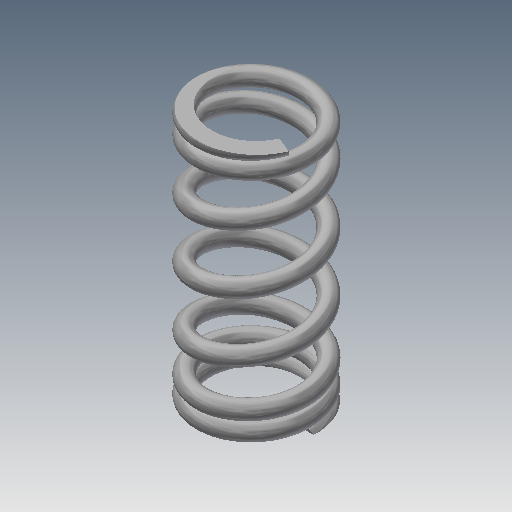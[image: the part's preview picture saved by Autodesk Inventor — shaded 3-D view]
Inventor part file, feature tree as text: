
AUTODESK INVENTOR PART (.ipt)
format: ipt  version: 2017 (Build 210142000, 142)  size: 893,952 bytes
history: native  units: mm
features: other x67, extrude x8, helix x5, sketch x3, sweep x2, plane x1
ambient origin geometry x8: Origin, YZ Plane, XZ Plane, XY Plane, X Axis, Y Axis, Z Axis, Center Point
bodies: Solid1 (feature_tree)
feature tree (86):
  other  "Main Coil Path(Right)"
  other  "Section Work Plane(Right)"
  other  "Start Work Plane(Right)"
  other  "End Work Plane(Right)"
  other  "End Cut Work Plane(Right)"
  other  "Start Cut Work Plane(Right)"
  other  "Plain Ends Cut Work Plane 1(Right)"
  other  "Plain Ends Cut Work Plane 2(Right)"
  sweep  "Main Coil Feature(R)"
  other  "Start Transition Coil 1(Right)"
  helix  "Coil  Start Transition 2(R)"  [1 undecoded]
  helix  "Coil  Start Transition 3(R)"  [1 undecoded]
  helix  "Coil  Start Transition 4(R)"  [1 undecoded]
  other  "Start Ends Coil(Right)"
  extrude  "Start Cut Feature(Right)"  Depth=10.0mm
  other  "End Transition Coil 1(Right)"
  other  "End Transition Coil 2(Right)"
  other  "End Transition Coil 3(Right)"
  other  "End Transition Coil 4(Right)"
  other  "End Coil(Right)"
  extrude  "End Cut Feature(Right)"  Depth=10.0mm
  extrude  "Plain Ends Cut Feature 1(Right)"  Depth=10.0mm
  extrude  "Plain Ends Cut  2(R)"  Depth=10.0mm TaperAngle=0.0deg
  other  "Main Coil Path(Left)"
  other  "Section Work Plane(Left)"
  other  "Start Work Plane(Left)"
  other  "End Work Plane(Left)"
  other  "End Cut Work Plane(Left)"
  other  "Start Cut Work Plane(Left)"
  other  "Plain Ends Cut Work Plane 1(Left)"
  other  "Plain Ends Cut Work Plane 2(Left)"
  sweep  "Main Coil Feature(L)"
  other  "Start Transition Coil 1(Left)"
  other  "Start Transition Coil 2(Left)"
  other  "Start Transition Coil 3(Left)"
  other  "Start Transition Coil 4(Left)"
  other  "Start Ends Coil(Left)"
  extrude  "Start Cut Feature(Left)"  Depth=10.0mm TaperAngle=0.0deg
  other  "End Transition Coil 1(Left)"
  other  "End Transition Coil 2(Left)"
  other  "End Transition Coil 3(Left)"
  other  "End Transition Coil 4(Left)"
  other  "End Coil(Left)"
  extrude  "End Cut Feature(Left)"  Depth=10.0mm
  extrude  "Cut Plain Ends Cut 1(L)"  TaperAngle=0.0deg  [1 undecoded]
  extrude  "Cut Plain Ends Cut 2(L)"  TaperAngle=0.0deg  [1 undecoded]
  other  "iMate Based Work Plane"
  other  "Preview Center Point"
  other  "Preview X Axis"
  other  "Path Section Sketch(Right)"
  other  "Srf1"
  helix  "Coil Section Sketch(Right)"  [1 undecoded]
  other  "Start Transition Coil Sketch 1(Right)"
  sketch  "Sketch  Start Transition 2(R)"  dims[d0=0.25mm d2=3.484629mm d3=10.0mm d4=26.875mm]
  sketch  "Sketch  Start Transition 3(R)"  dims[d5=0.0mm d6=90.0deg d7=90.0deg d8=0.0mm d9=0.0mm d12=2.448943mm d13=-3.186113mm d14=1.0mm]
  sketch  "Sketch  Start Transition 4(R)"  dims[d15=0.0mm d16=2.863472mm d17=10.0mm d18=2.5mm d19=0.0mm d20=90.0deg d21=90.0deg d22=0.0mm d23=0.0mm d24=2.242315mm d25=10.0mm d26=2.5mm d27=0.0mm d28=90.0deg d29=90.0deg d30=0.0mm d31=0.0mm d32=1.621157mm d33=10.0mm d34=2.5mm d35=0.0mm d36=90.0deg d37=90.0deg d38=0.0mm d39=0.0mm d40=1.0mm d41=10.0mm d42=2.5mm d43=0.0mm d44=90.0deg d45=90.0deg d46=0.0mm d47=0.0mm d48=2.863472mm d49=10.0mm d50=1.875mm d51=0.0mm d52=90.0deg d53=90.0deg d54=0.0mm d55=0.0mm d56=2.242315mm d57=10.0mm d58=1.875mm d59=0.0mm d60=90.0deg d61=90.0deg d62=0.0mm d63=0.0mm d64=1.621157mm d65=10.0mm d66=1.875mm d67=0.0mm d68=90.0deg d69=90.0deg d70=0.0mm d71=0.0mm d72=1.0mm d73=10.0mm d74=1.875mm d75=0.0mm d76=90.0deg d77=90.0deg d78=0.0mm d79=0.0mm d81=10.0mm d82=15.0mm d83=0.0mm d84=90.0deg d85=90.0deg d86=0.0mm d87=0.0mm d88=1.016944mm d89=10.0mm d90=10.0mm d91=0.0mm d92=90.0deg d93=90.0deg d94=0.0mm d95=0.0mm d96=7.0mm d97=1.016944mm d98=0.0mm d99=7.0mm d100=1.016944mm d101=0.0mm d102=0.0mm d103=0.0mm d104=0.0mm d105=0.0mm d106=0.0mm d108=0.0mm d112=0.0mm d113=0.0mm d114=0.0mm d121=0.271039mm d131=0.0mm d132=0.0mm d133=0.0mm d134=0.0mm d135=0.25mm d137=3.484629mm d138=10.0mm d139=26.875mm d140=0.0mm d141=90.0deg d142=90.0deg d143=0.0mm d144=0.0mm d145=2.448943mm d146=-3.186113mm d147=0.271039mm d148=0.016803mm d149=1.0mm d150=0.0mm d151=0.0mm d152=2.863472mm d153=10.0mm d154=2.5mm d155=0.0mm d156=90.0deg d157=90.0deg d158=0.0mm d159=0.0mm d160=2.242315mm d161=10.0mm d162=2.5mm d163=0.0mm d164=90.0deg d165=90.0deg d166=0.0mm d167=0.0mm d168=1.621157mm d169=10.0mm d170=2.5mm d171=0.0mm d172=90.0deg d173=90.0deg d174=0.0mm d175=0.0mm d176=1.0mm d177=10.0mm d178=2.5mm d179=0.0mm d180=90.0deg d181=90.0deg d182=0.0mm d183=0.0mm d184=10.0mm d185=10.0mm d186=10.0mm d187=10.0mm d188=1.016944mm d189=10.0mm d190=15.0mm d191=0.0mm d192=90.0deg d193=90.0deg d194=0.0mm d195=0.0mm d196=10.0mm d197=7.0mm d198=1.016944mm d199=0.0mm d200=10.0mm d201=2.863472mm d202=10.0mm d203=1.875mm d204=0.0mm d205=90.0deg d206=90.0deg d207=0.0mm d208=0.0mm d209=10.0mm d210=2.242315mm d211=10.0mm d212=1.875mm d213=0.0mm d214=90.0deg d215=90.0deg d216=0.0mm d217=0.0mm d218=1.621157mm d219=10.0mm d220=1.875mm d221=0.0mm d222=90.0deg d223=90.0deg d224=0.0mm d225=0.0mm d226=1.0mm d227=10.0mm d228=1.875mm d229=0.0mm d230=90.0deg d231=90.0deg d232=0.0mm d233=0.0mm d234=10.0mm d235=10.0mm d236=10.0mm d237=1.016944mm d238=10.0mm d239=10.0mm d240=0.0mm d241=90.0deg d242=90.0deg d243=0.0mm d244=0.0mm d245=7.0mm d246=1.016944mm d247=0.0mm d248=10.0mm d249=10.0mm d254=7.0mm d255=10.0mm d256=0.0mm d257=20.0mm d258=-0.016803mm d259=7.0mm d260=10.0mm d261=0.0mm d262=10.0mm d263=7.0mm d264=10.0mm d265=0.0mm d266=10.0mm d267=0.0mm d270=-3.061113mm d271=0.0mm d272=7.0mm d273=10.0mm d274=0.0mm d275=20.0mm d276=-157.079633mm d277=6.0mm d278=6.0mm d279=0.0mm d280=0.0mm]
  other  "End Transition Coil Sketch 1(Right)"
  other  "End Transition Coil Sketch 2(Right)"
  other  "End Transition Coil Sketch 3(Right)"
  other  "End Transition Coil Sketch 4(Right)"
  other  "Start Ends Skecth(Right)"
  other  "End Coil Skecth(Right)"
  other  "End Cut Sketch(Right)"
  other  "Start Cut Sketch(Right)"
  other  "Path Section Sketch(Left)"
  other  "Srf2"
  helix  "Coil Section Sketch(Left)"  [1 undecoded]
  other  "Start Transition Coil Sketch 1(Left)"
  other  "Start Transition Coil Sketch 2(Left)"
  other  "Start Transition Coil Sketch 3(Left)"
  other  "Start Transition Coil Sketch 4(Left)"
  other  "Start Ends Skecth(Left)"
  other  "Start Cut Sketch(Left)"
  other  "End Transition Coil Sketch 1(Left)"
  other  "End Transition Coil Sketch 2(Left)"
  other  "End Transition Coil Sketch 3(Left)"
  other  "End Transition Coil Sketch 4(Left)"
  other  "End Coil Skecth(Left)"
  other  "End Cut Sketch(Left)"
  other  "Plain Ends Cut Sketch 2(Left)"
  other  "Plain Ends Cut Sketch 2(Right)"
  other  "Plain Ends Cut Sketch 1(Right)"
  other  "Plain Ends Cut Sketch 1(Left)"
  plane  "Work Plane Start Section"
  other  "Basic Curve(Right)"
  other  "Basic Curve(Left)"
note: 7 required parameter values undecoded (feature->parameter linkage not recoverable at this tier; creation-order binding heuristic only, values carry confidence <= 0.55)
